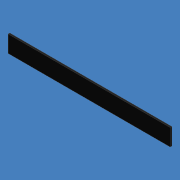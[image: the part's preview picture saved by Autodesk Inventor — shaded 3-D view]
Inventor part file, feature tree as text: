
AUTODESK INVENTOR PART (.ipt)
format: ipt  version: 2011 (Build 150239000, 239)  size: 73,728 bytes
history: native  units: mm (DEFAULTED — no unit token found)
features: extrude x1, sketch x1
ambient origin geometry x8: Origin, YZ Plane, XZ Plane, XY Plane, X Axis, Y Axis, Z Axis, Center Point
bodies: Solid1 (feature_tree)
feature tree (2):
  extrude  "Extrusion1"  Depth=19.05mm
  sketch  "Sketch1"  dims[d0=184.15mm d1=19.05mm d2=1.905mm d3=0.0mm]
